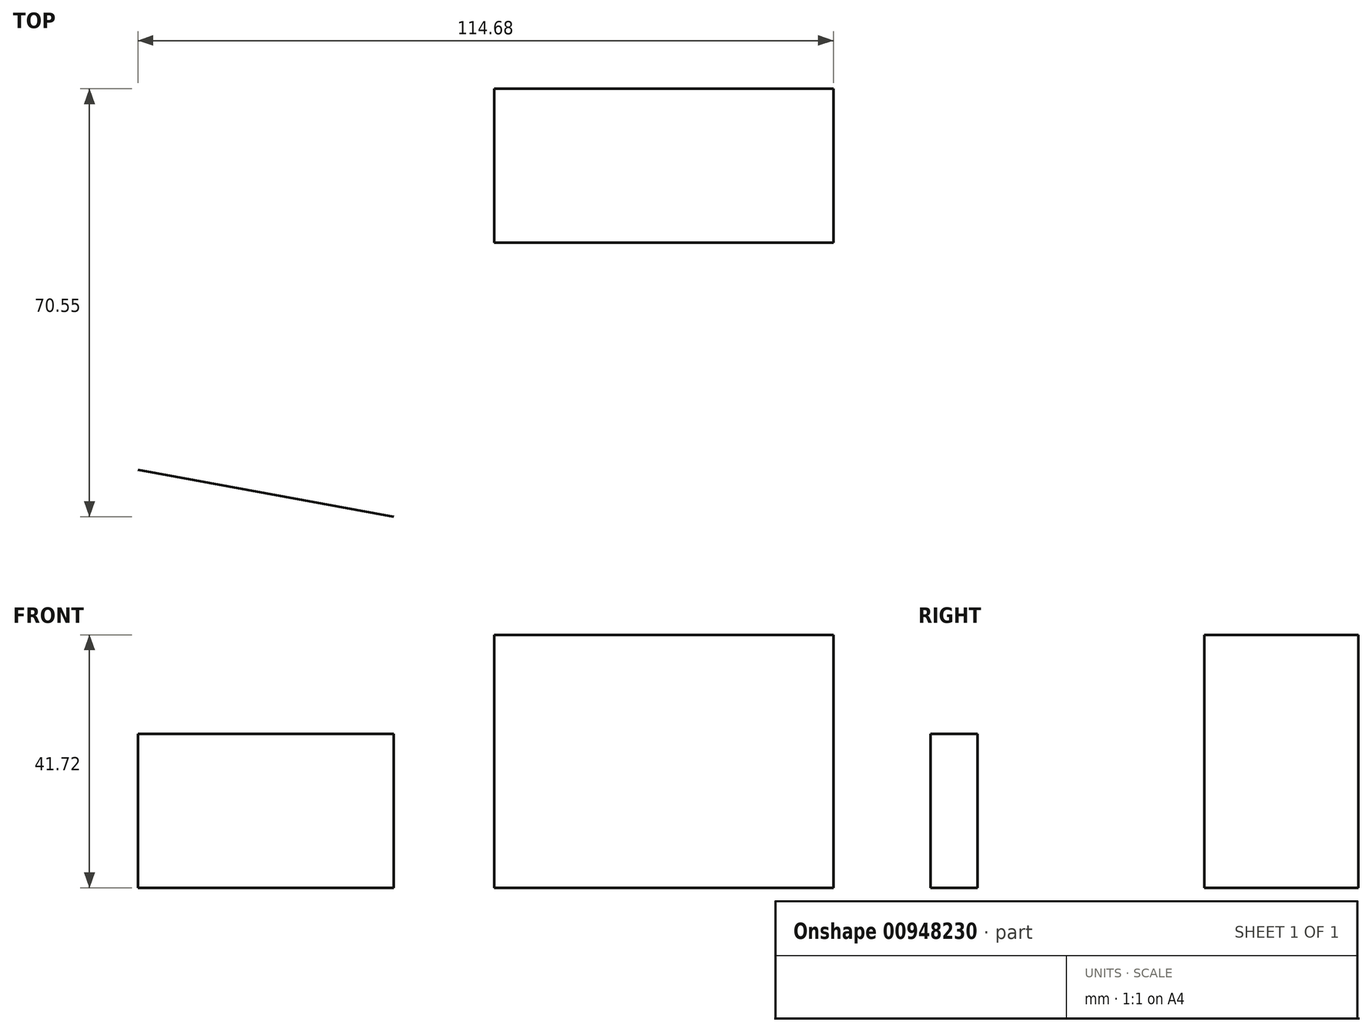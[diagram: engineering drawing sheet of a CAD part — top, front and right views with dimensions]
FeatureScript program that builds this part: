
annotation { "Feature Type Name" : "Feature", "Feature Type Description" : "" }
export const myFeature = defineFeature(function(context is Context, id is Id, definition is map)
    precondition{}
    {
        {
            var Q0;
            Q0=qCreatedBy(makeId("Front.planeOp"),FACE);
            var sketch = newSketch(context, id + "F0", { "sketchPlane" : qUnion([Q0])});
            skLineSegment(sketch, "E0.bottom", {"start": v(0, 0) * mm, "end": v(55.91, 0) * mm});
            skLineSegment(sketch, "E0.top", {"start": v(0, 41.72) * mm, "end": v(55.91, 41.72) * mm});
            skLineSegment(sketch, "E0.left", {"start": v(0, 0) * mm, "end": v(0, 41.72) * mm});
            skLineSegment(sketch, "E0.right", {"start": v(55.91, 0) * mm, "end": v(55.91, 41.72) * mm});
            skSolve(sketch);
        }
        {
            var Q0;
            Q0=qCreatedBy(makeId("Top.planeOp"),FACE);
            var sketch = newSketch(context, id + "F1", { "sketchPlane" : qUnion([Q0])});
            skLineSegment(sketch, "E1", {"start": v(-58.77, -62.8) * mm, "end": v(-16.62, -70.55) * mm});
            skSolve(sketch);
        }
        {
            var Q0;
            Q0 = qSketchRegion(id + "F1", true);
            var Q1;
            Q1=sQuery(id+"F1.wireOp",EDGE,"E1");
            extrude(context, id + "F2", {"entities" : qUnion([Q0]), "bodyType" : ToolBodyType.SURFACE, "surfaceEntities" : qUnion([Q1]), "depth" : 25.4 * mm, "offsetDistance" : 25.4 * mm});
        }
        {
            var Q0;
            Q0 = qSketchRegion(id + "F0", true);
            var Q1;
            Q1=sQuery(id+"F0.wireOp",EDGE,"E0.top");
            var Q2;
            Q2=sQuery(id+"F0.wireOp",EDGE,"E0.right");
            var Q3;
            Q3=sQuery(id+"F0.wireOp",EDGE,"E0.left");
            var Q4;
            Q4=sQuery(id+"F0.wireOp",EDGE,"E0.bottom");
            extrude(context, id + "F3", {"entities" : qUnion([Q0]), "bodyType" : ToolBodyType.SURFACE, "surfaceEntities" : qUnion([Q1, Q2, Q3, Q4]), "depth" : 25.4 * mm, "offsetDistance" : 25.4 * mm});
        }
    });
